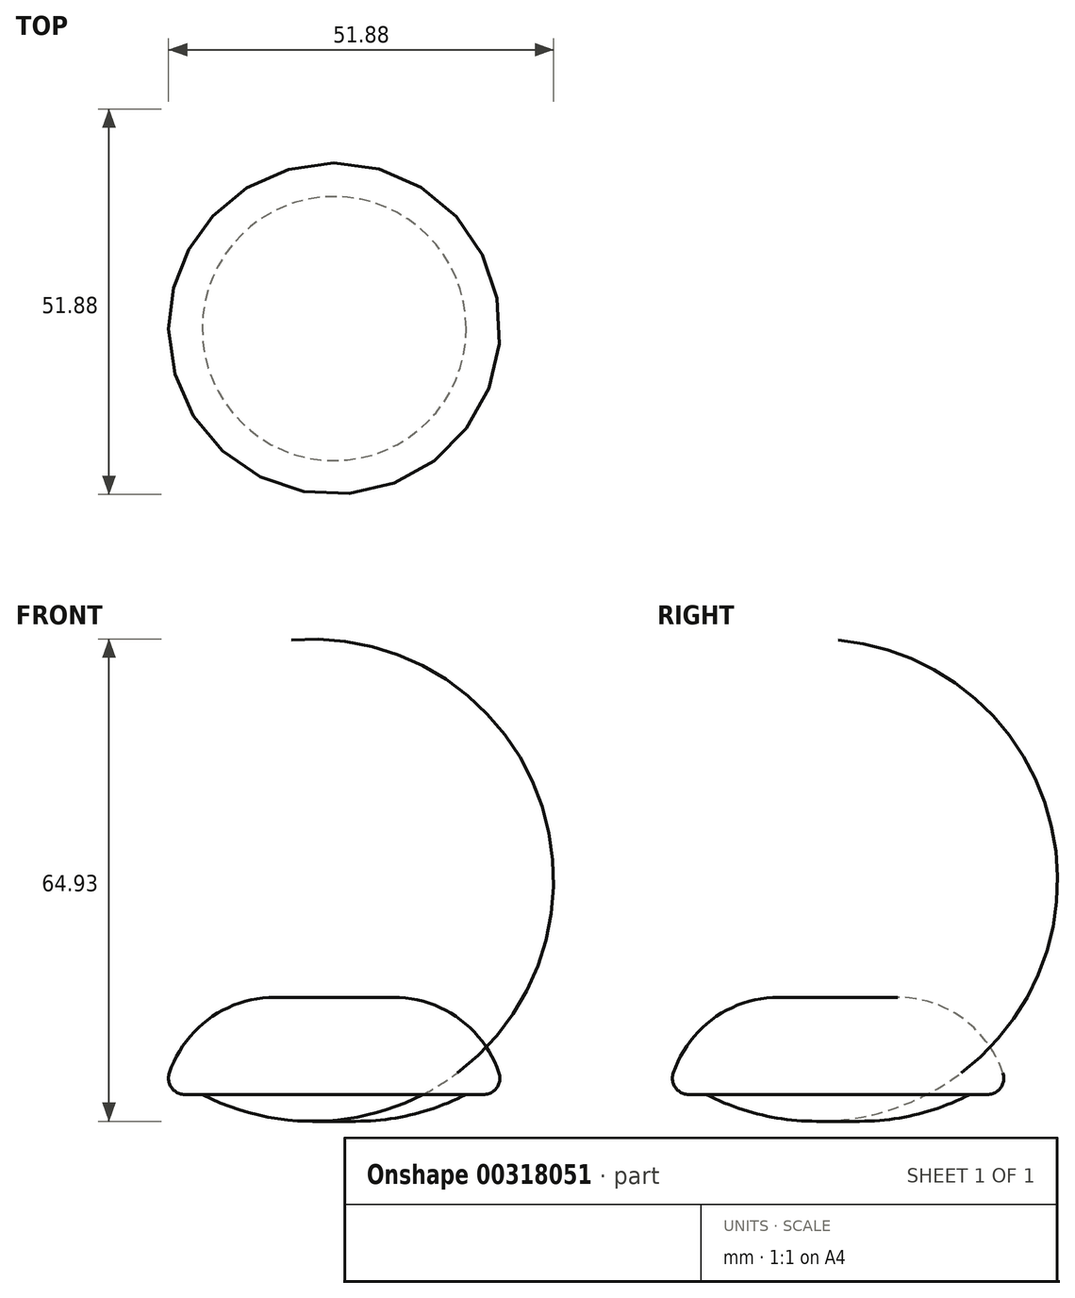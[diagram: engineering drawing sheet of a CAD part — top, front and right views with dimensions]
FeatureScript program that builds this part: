
annotation { "Feature Type Name" : "Feature", "Feature Type Description" : "" }
export const myFeature = defineFeature(function(context is Context, id is Id, definition is map)
    precondition{}
    {
        {
            var Q0;
            Q0=qCreatedBy(makeId("Front.planeOp"),FACE);
            var sketch = newSketch(context, id + "F0", { "sketchPlane" : qUnion([Q0])});
            skLineSegment(sketch, "E0", {"start": v(0, 0) * mm, "end": v(8, 0) * mm});
            skArc(sketch, "E1", {"start": v(22.2, -10.17) * mm, "mid": v(16.73, -2.8) * mm, "end": v(8, 0) * mm});
            skArc(sketch, "E2", {"start": v(20.12, -13.08) * mm, "mid": v(21.9, -12.16) * mm, "end": v(22.2, -10.17) * mm});
            skLineSegment(sketch, "E3", {"start": v(20.12, -13.08) * mm, "end": v(0, -13.08) * mm});
            skLineSegment(sketch, "E4", {"start": v(13.72, -14.83) * mm, "end": v(0, -14.83) * mm});
            skPoint(sketch, "E5.endSnap0", {"position": v(4, 0) * mm});
            skArc(sketch, "E6", {"start": v(0, -16.56) * mm, "mid": v(9.13, -16.08) * mm, "end": v(17.77, -13.08) * mm});
            skLineSegment(sketch, "E7", {"start": v(0, -28.75) * mm, "end": v(0, 7.56) * mm});
            skSolve(sketch);
        }
        {
            var Q0;
            {var subQ3=sQuery(id+"F0.wireOp",EDGE,"E0");Q0=makeQuery(id+"F0.imprint","IMPRINT",FACE,{"disambiguationData":[TD([[makeQuery(id+"F0.imprint","IMPRINT",EDGE,{"derivedFrom":subQ3}),-1.0]])]});}
            var Q1;
            {var subQ5=sQuery(id+"F0.wireOp",EDGE,"E4");Q1=makeQuery(id+"F0.imprint","IMPRINT",FACE,{"disambiguationData":[TD([[makeQuery(id+"F0.imprint","IMPRINT",EDGE,{"derivedFrom":subQ5}),-1.0]])]});}
            var Q2;
            {var subQ0=sQuery(id+"F0.wireOp",EDGE,"E4");Q2=makeQuery(id+"F0.imprint","IMPRINT",FACE,{"disambiguationData":[TD([[makeQuery(id+"F0.imprint","IMPRINT",EDGE,{"derivedFrom":subQ0}),1.0]])]});}
            var Q3;
            Q3=sQuery(id+"F0.wireOp",EDGE,"E7");
            revolve(context, id + "F1", {"entities" : qUnion([Q0, Q1, Q2]), "axis" : qUnion([Q3]), "revolveType" : RevolveType.FULL});
        }
    });
